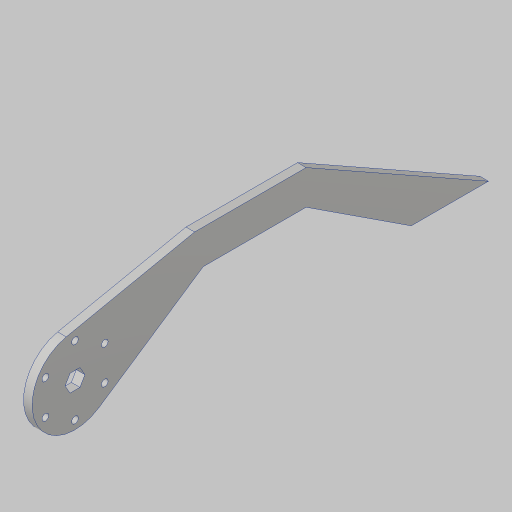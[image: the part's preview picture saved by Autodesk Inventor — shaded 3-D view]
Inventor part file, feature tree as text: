
AUTODESK INVENTOR PART (.ipt)
format: ipt  version: 2023.5 (Build 275446000, 446)  size: 130,560 bytes
history: native  units: in
note: dims shown in document units (in); Inventor stores cm internally (conversion verified against a paired STEP export)
features: sketch x3, extrude x1, hole x1
ambient origin geometry x8: Origin, YZ Plane, XZ Plane, XY Plane, X Axis, Y Axis, Z Axis, Center Point
bodies: Solid1 (feature_tree)
feature tree (5):
  sketch  "Sketch1"  dims[d0=2.5in d2=5.0in]
  extrude  "Extrusion1"  Depth=5.0in
  hole  "Hole1"  [1 undecoded]
  sketch  "Sketch2"  dims[d3=2.3037in d4=0.75in]
  sketch  "Sketch3"  dims[d5=6.385in d6=8.0in d7=1.0in d8=0.25in d9=3.0in d10=1.0in d11=3.25in d12=0.5in d13=2.25in d14=0.25in d15=0.0in d16=2.0in d17=2.3622in d19=360.0deg d21=0.201in d22=0.38in d23=0.385in d24=0.25in d25=0.5635in d26=1.0in d27=0.8108in]
note: 1 required parameter value undecoded (feature->parameter linkage not recoverable at this tier; creation-order binding heuristic only, values carry confidence <= 0.55)
